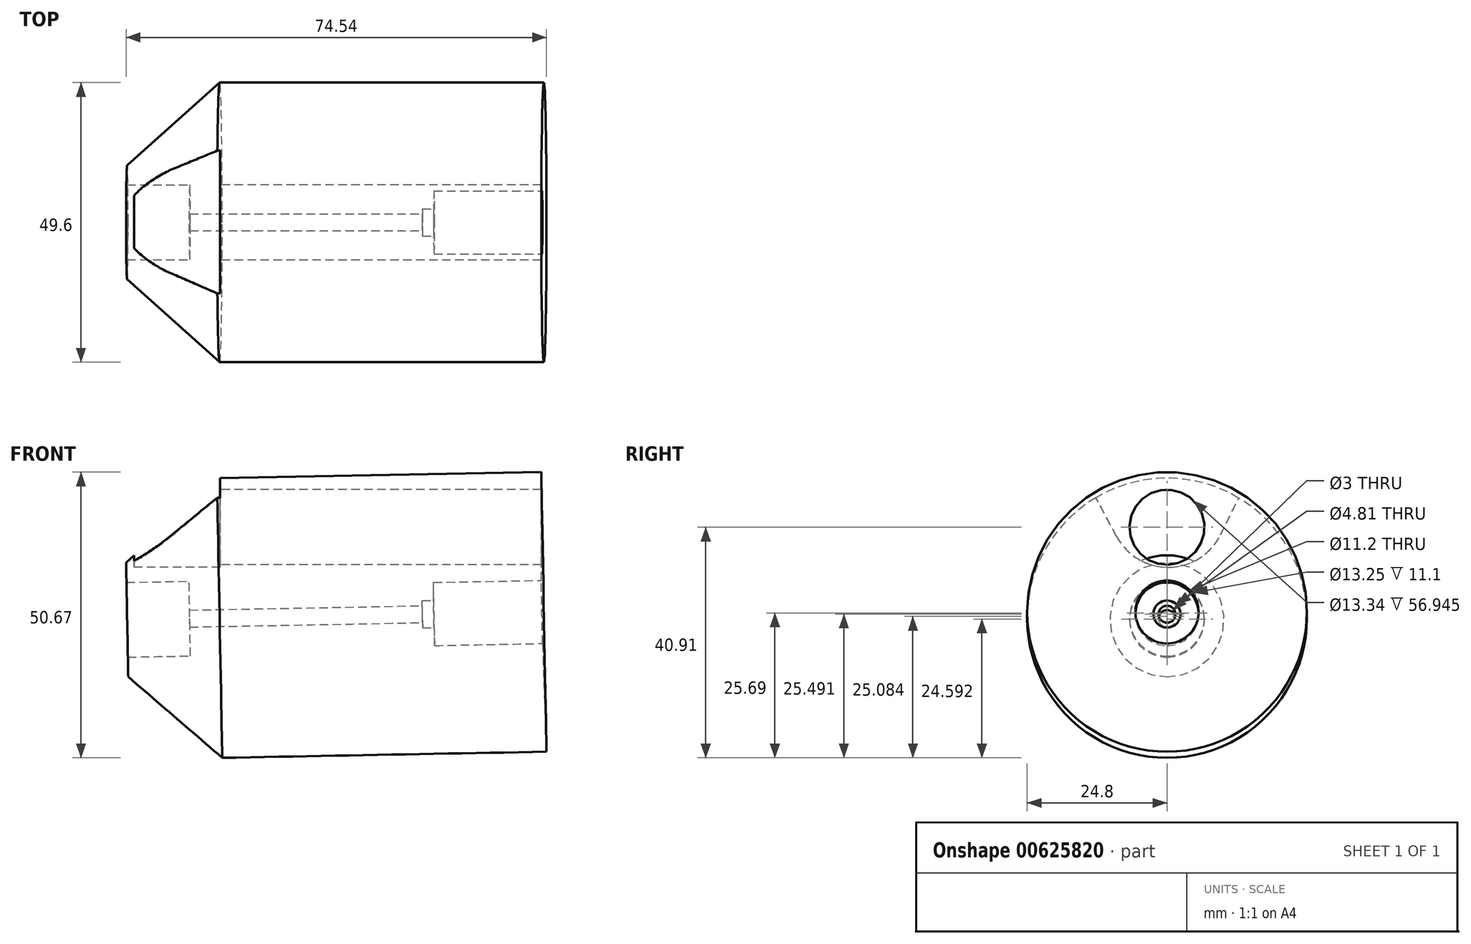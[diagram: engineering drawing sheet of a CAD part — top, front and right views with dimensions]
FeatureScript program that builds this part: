
annotation { "Feature Type Name" : "Feature", "Feature Type Description" : "" }
export const myFeature = defineFeature(function(context is Context, id is Id, definition is map)
    precondition{}
    {
        {
            var Q0;
            Q0=qCreatedBy(makeId("Front.planeOp"),FACE);
            var sketch = newSketch(context, id + "F0", { "sketchPlane" : qUnion([Q0])});
            skLineSegment(sketch, "E0", {"start": v(41.04, 0) * mm, "end": v(-163.18, -3.84) * mm, "construction": true});
            skLineSegment(sketch, "E1", {"start": v(-35.16, 0.07) * mm, "end": v(6.09, 0.84) * mm});
            skLineSegment(sketch, "E2", {"start": v(6.09, 0.84) * mm, "end": v(6.09, 1.75) * mm});
            skLineSegment(sketch, "E3", {"start": v(6.09, 1.75) * mm, "end": v(8.09, 1.79) * mm});
            skLineSegment(sketch, "E4", {"start": v(8.09, 1.79) * mm, "end": v(8.09, 4.98) * mm});
            skLineSegment(sketch, "E5", {"start": v(8.09, 4.98) * mm, "end": v(27.18, 5.34) * mm});
            skLineSegment(sketch, "E6", {"start": v(27.18, 5.34) * mm, "end": v(27.18, 24.54) * mm});
            skLineSegment(sketch, "E7", {"start": v(27.18, 24.54) * mm, "end": v(-30.3, 23.46) * mm});
            skLineSegment(sketch, "E8", {"start": v(-30.3, 23.46) * mm, "end": v(-46.42, 8.48) * mm});
            skLineSegment(sketch, "E9", {"start": v(-46.42, 8.48) * mm, "end": v(-46.35, 4.98) * mm});
            skLineSegment(sketch, "E10", {"start": v(-46.35, 4.98) * mm, "end": v(-35.25, 5.19) * mm});
            skLineSegment(sketch, "E11", {"start": v(-35.25, 5.19) * mm, "end": v(-35.16, 0.07) * mm});
            skSolve(sketch);
        }
        {
            var Q0;
            Q0=makeQuery(id+"F0.imprint","IMPRINT",FACE,{"disambiguationData":[TD([[makeQuery(id+"F0.imprint","IMPRINT",EDGE,{"derivedFrom":sQuery(id+"F0.wireOp",EDGE,"E1")}),1.0]])]});
            var Q1;
            Q1=sQuery(id+"F0.wireOp",EDGE,"E0");
            revolve(context, id + "F1", {"entities" : qUnion([Q0]), "axis" : qUnion([Q1]), "revolveType" : RevolveType.FULL});
        }
        {
            var Q0;
            Q0=qCreatedBy(makeId("Right.planeOp"),FACE);
            cPlane(context, id + "F2", {"entities" : qUnion([Q0]), "cplaneType" : CPlaneType.OFFSET, "offset" : 45 * mm, "oppositeDirection" : true, "width" : 150 * mm, "height" : 150 * mm});
        }
        {
            var Q0;
            Q0=qCreatedBy(id+"F2.planeOp",FACE);
            var sketch = newSketch(context, id + "F3", { "sketchPlane" : qUnion([Q0])});
            skCircle(sketch, "E12", {"center": v(0, 14.78) * mm, "radius": 6.67 * mm});
            skArc(sketch, "E13", {"start": v(-8.96, 13.17) * mm, "mid": v(0.35, 7.67) * mm, "end": v(9.5, 13.44) * mm});
            skLineSegment(sketch, "E14", {"start": v(-8.96, 13.17) * mm, "end": v(-21.62, 36.97) * mm});
            skLineSegment(sketch, "E15", {"start": v(-21.62, 36.97) * mm, "end": v(18.2, 36.97) * mm});
            skLineSegment(sketch, "E16", {"start": v(9.5, 13.44) * mm, "end": v(21.15, 36.97) * mm});
            skLineSegment(sketch, "E17", {"start": v(21.15, 36.97) * mm, "end": v(18.2, 36.97) * mm});
            skSolve(sketch);
        }
        {
            var Q0;
            Q0=makeQuery(id+"F3.imprint","IMPRINT",FACE,{"disambiguationData":[TD([[makeQuery(id+"F3.imprint","IMPRINT",EDGE,{"derivedFrom":sQuery(id+"F3.wireOp",EDGE,"E12")}),1.0]])]});
            var Q1;
            Q1=sQuery(id+"F3.wireOp",EDGE,"E12");
            extrude(context, id + "F4", {"entities" : qUnion([Q0]), "operationType" : NewBodyOperationType.REMOVE, "surfaceEntities" : qUnion([Q1]), "endBound" : BoundingType.THROUGH_ALL, "depth" : 25 * mm, "offsetDistance" : 25 * mm});
        }
        {
            var Q0;
            Q0=makeQuery(id+"F3.imprint","IMPRINT",FACE,{"disambiguationData":[TD([[makeQuery(id+"F3.imprint","IMPRINT",EDGE,{"derivedFrom":sQuery(id+"F3.wireOp",EDGE,"E12")}),-1.0]])]});
            extrude(context, id + "F5", {"entities" : qUnion([Q0]), "operationType" : NewBodyOperationType.REMOVE, "depth" : 15.26 * mm, "offsetDistance" : 25 * mm});
        }
    });
